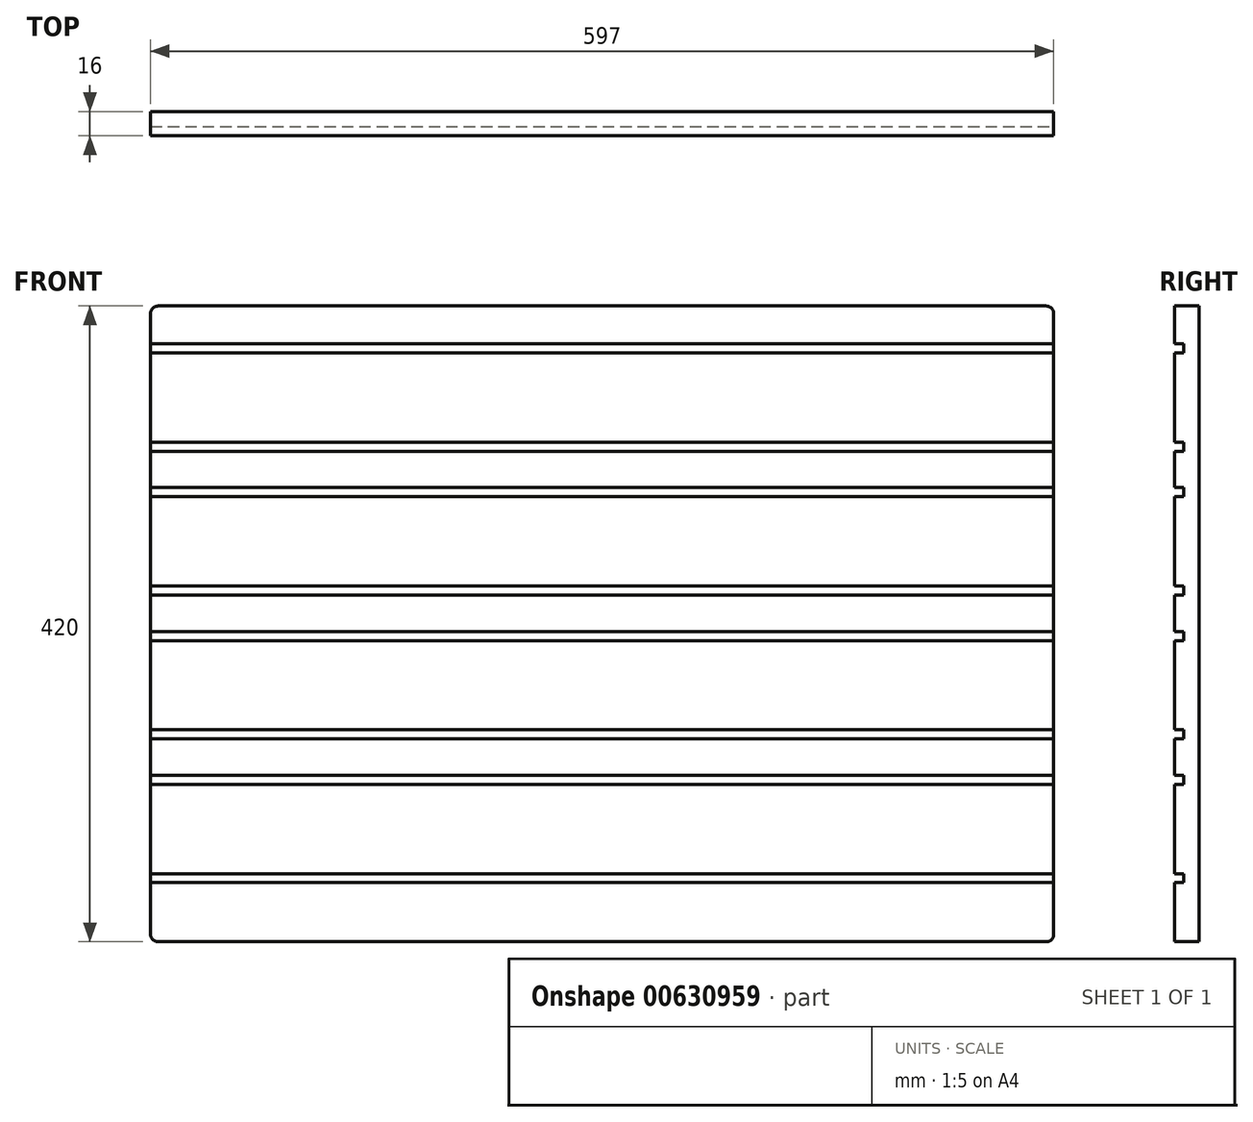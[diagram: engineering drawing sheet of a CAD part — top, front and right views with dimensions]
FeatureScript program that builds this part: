
annotation { "Feature Type Name" : "Feature", "Feature Type Description" : "" }
export const myFeature = defineFeature(function(context is Context, id is Id, definition is map)
    precondition{}
    {
        {
            var Q0;
            Q0=qCreatedBy(makeId("Front.planeOp"),FACE);
            var sketch = newSketch(context, id + "F0", { "sketchPlane" : qUnion([Q0])});
            skLineSegment(sketch, "E0.bottom", {"start": v(303.08, -205) * mm, "end": v(-283.92, -205) * mm});
            skLineSegment(sketch, "E0.top", {"start": v(303.08, 215) * mm, "end": v(-283.92, 215) * mm});
            skLineSegment(sketch, "E0.left", {"start": v(308.08, -200) * mm, "end": v(308.08, 210) * mm});
            skLineSegment(sketch, "E0.right", {"start": v(-288.92, -200) * mm, "end": v(-288.92, 210) * mm});
            skPoint(sketch, "E1.visualSharp", {"position": v(-288.92, -205) * mm});
            skArc(sketch, "E1.filletArc", {"start": v(-288.92, -200) * mm, "mid": v(-287.45, -203.54) * mm, "end": v(-283.92, -205) * mm});
            skPoint(sketch, "E2.visualSharp", {"position": v(-288.92, 215) * mm});
            skArc(sketch, "E2.filletArc", {"start": v(-283.92, 215) * mm, "mid": v(-287.45, 213.54) * mm, "end": v(-288.92, 210) * mm});
            skPoint(sketch, "E3.visualSharp", {"position": v(308.08, 215) * mm});
            skArc(sketch, "E3.filletArc", {"start": v(308.08, 210) * mm, "mid": v(306.62, 213.54) * mm, "end": v(303.08, 215) * mm});
            skPoint(sketch, "E4.visualSharp", {"position": v(308.08, -205) * mm});
            skArc(sketch, "E4.filletArc", {"start": v(303.08, -205) * mm, "mid": v(306.62, -203.54) * mm, "end": v(308.08, -200) * mm});
            skSolve(sketch);
        }
        {
            var Q0;
            Q0 = qSketchRegion(id + "F0", true);
            extrude(context, id + "F1", {"entities" : qUnion([Q0]), "depth" : 16 * mm, "offsetDistance" : 25 * mm});
        }
        {
            var Q0;
            Q0=makeQuery(id+"F1.opExtrude","CAP_FACE",FACE,{"disambiguationData":[OSD([sQuery(id+"F0.wireOp",EDGE,"E0.bottom"),sQuery(id+"F0.wireOp",EDGE,"E0.top"),sQuery(id+"F0.wireOp",EDGE,"E0.left"),sQuery(id+"F0.wireOp",EDGE,"E0.right")])],"isStart":false});
            var sketch = newSketch(context, id + "F2", { "sketchPlane" : qUnion([Q0])});
            skLineSegment(sketch, "E5.bottom", {"start": v(-288.92, 190) * mm, "end": v(308.08, 190) * mm});
            skLineSegment(sketch, "E5.top", {"start": v(-288.92, 184) * mm, "end": v(308.08, 184) * mm});
            skLineSegment(sketch, "E5.left", {"start": v(-288.92, 190) * mm, "end": v(-288.92, 184) * mm});
            skLineSegment(sketch, "E5.right", {"start": v(308.08, 190) * mm, "end": v(308.08, 184) * mm});
            skLineSegment(sketch, "E6.bottom", {"start": v(-288.92, 125) * mm, "end": v(308.08, 125) * mm});
            skLineSegment(sketch, "E6.top", {"start": v(-288.92, 119) * mm, "end": v(308.08, 119) * mm});
            skLineSegment(sketch, "E6.left", {"start": v(-288.92, 125) * mm, "end": v(-288.92, 119) * mm});
            skLineSegment(sketch, "E6.right", {"start": v(308.08, 125) * mm, "end": v(308.08, 119) * mm});
            skLineSegment(sketch, "E7.bottom", {"start": v(-288.92, 95) * mm, "end": v(308.08, 95) * mm});
            skLineSegment(sketch, "E7.top", {"start": v(-288.92, 89) * mm, "end": v(308.08, 89) * mm});
            skLineSegment(sketch, "E7.left", {"start": v(-288.92, 95) * mm, "end": v(-288.92, 89) * mm});
            skLineSegment(sketch, "E7.right", {"start": v(308.08, 95) * mm, "end": v(308.08, 89) * mm});
            skLineSegment(sketch, "E8.bottom", {"start": v(-288.92, 0) * mm, "end": v(308.08, 0) * mm});
            skLineSegment(sketch, "E8.top", {"start": v(-288.92, -6) * mm, "end": v(308.08, -6) * mm});
            skLineSegment(sketch, "E8.left", {"start": v(-288.92, 0) * mm, "end": v(-288.92, -6) * mm});
            skLineSegment(sketch, "E8.right", {"start": v(308.08, 0) * mm, "end": v(308.08, -6) * mm});
            skLineSegment(sketch, "E9.bottom", {"start": v(-288.92, -65) * mm, "end": v(308.08, -65) * mm});
            skLineSegment(sketch, "E9.top", {"start": v(-288.92, -71) * mm, "end": v(308.08, -71) * mm});
            skLineSegment(sketch, "E9.left", {"start": v(-288.92, -65) * mm, "end": v(-288.92, -71) * mm});
            skLineSegment(sketch, "E9.right", {"start": v(308.08, -65) * mm, "end": v(308.08, -71) * mm});
            skLineSegment(sketch, "E10.bottom", {"start": v(-288.92, -95) * mm, "end": v(308.08, -95) * mm});
            skLineSegment(sketch, "E10.top", {"start": v(-288.92, -101) * mm, "end": v(308.08, -101) * mm});
            skLineSegment(sketch, "E10.left", {"start": v(-288.92, -95) * mm, "end": v(-288.92, -101) * mm});
            skLineSegment(sketch, "E10.right", {"start": v(308.08, -95) * mm, "end": v(308.08, -101) * mm});
            skLineSegment(sketch, "E11.bottom", {"start": v(-288.92, 30) * mm, "end": v(308.08, 30) * mm});
            skLineSegment(sketch, "E11.top", {"start": v(-288.92, 24) * mm, "end": v(308.08, 24) * mm});
            skLineSegment(sketch, "E11.left", {"start": v(-288.92, 30) * mm, "end": v(-288.92, 24) * mm});
            skLineSegment(sketch, "E11.right", {"start": v(308.08, 30) * mm, "end": v(308.08, 24) * mm});
            skLineSegment(sketch, "E12.bottom", {"start": v(-288.92, -160) * mm, "end": v(308.08, -160) * mm});
            skLineSegment(sketch, "E12.top", {"start": v(-288.92, -166) * mm, "end": v(308.08, -166) * mm});
            skLineSegment(sketch, "E12.left", {"start": v(-288.92, -160) * mm, "end": v(-288.92, -166) * mm});
            skLineSegment(sketch, "E12.right", {"start": v(308.08, -160) * mm, "end": v(308.08, -166) * mm});
            skSolve(sketch);
        }
        {
            var Q0;
            Q0 = qSketchRegion(id + "F2", true);
            extrude(context, id + "F3", {"entities" : qUnion([Q0]), "operationType" : NewBodyOperationType.REMOVE, "oppositeDirection" : true, "depth" : 6 * mm, "offsetDistance" : 25 * mm});
        }
    });
